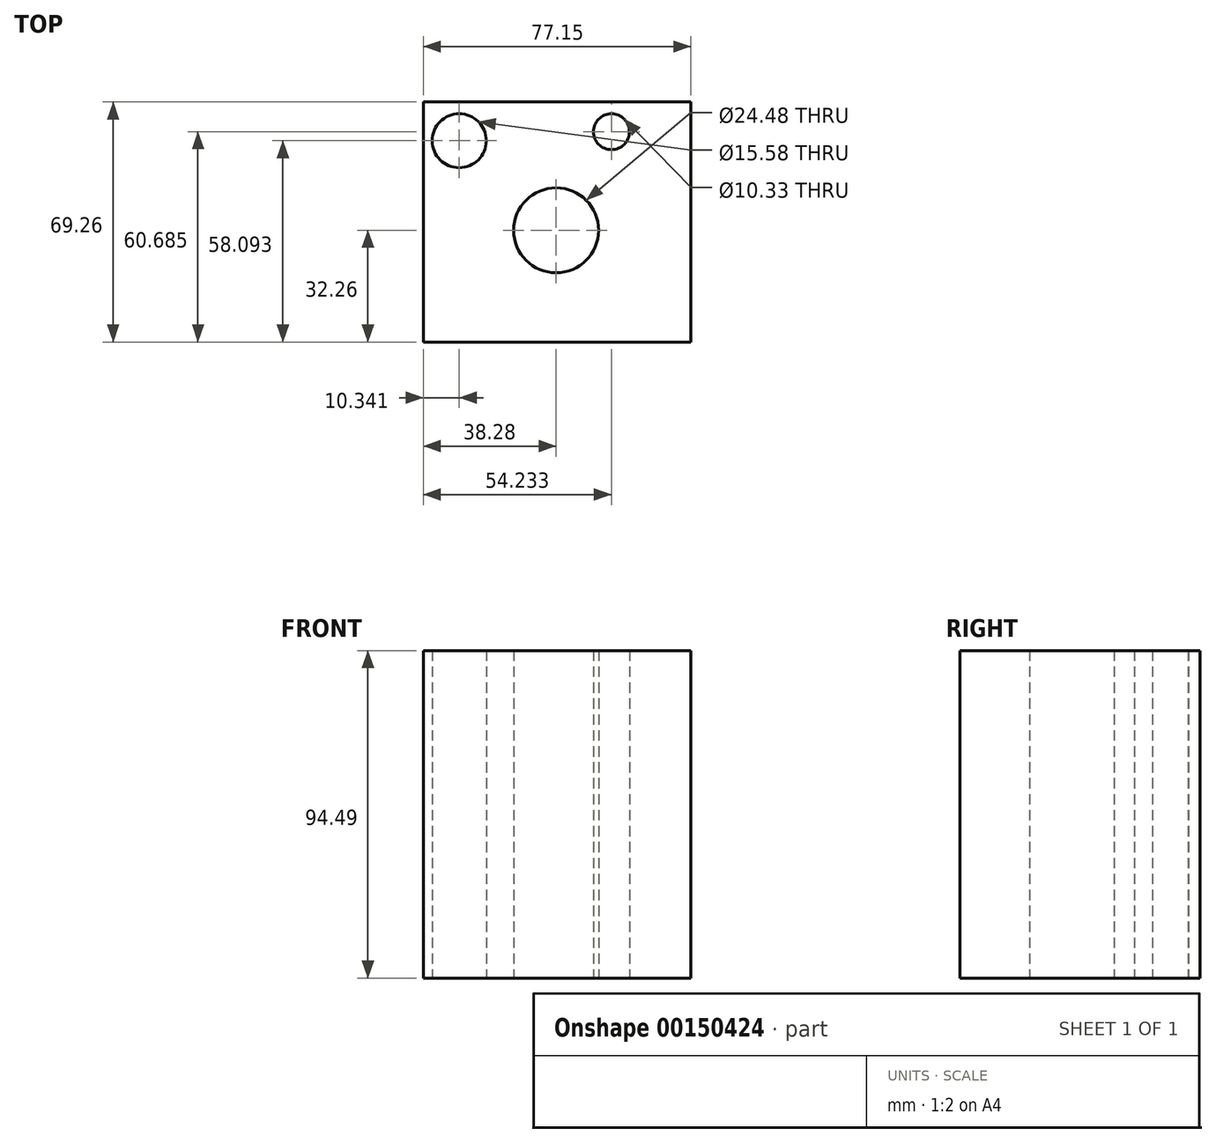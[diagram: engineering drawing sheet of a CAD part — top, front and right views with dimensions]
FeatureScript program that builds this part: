
annotation { "Feature Type Name" : "Feature", "Feature Type Description" : "" }
export const myFeature = defineFeature(function(context is Context, id is Id, definition is map)
    precondition{}
    {
        {
            var Q0;
            Q0=qCreatedBy(makeId("Top.planeOp"),FACE);
            var sketch = newSketch(context, id + "F0", { "sketchPlane" : qUnion([Q0])});
            skLineSegment(sketch, "E0.bottom", {"start": v(-38.28, 37) * mm, "end": v(38.87, 37) * mm});
            skLineSegment(sketch, "E0.top", {"start": v(-38.28, -32.26) * mm, "end": v(38.87, -32.26) * mm});
            skLineSegment(sketch, "E0.left", {"start": v(-38.28, 37) * mm, "end": v(-38.28, -32.26) * mm});
            skLineSegment(sketch, "E0.right", {"start": v(38.87, 37) * mm, "end": v(38.87, -32.26) * mm});
            skCircle(sketch, "E1", {"center": v(0, 0) * mm, "radius": 12.24 * mm});
            skCircle(sketch, "E2", {"center": v(-27.94, 25.83) * mm, "radius": 7.79 * mm});
            skCircle(sketch, "E3", {"center": v(15.95, 28.42) * mm, "radius": 5.17 * mm});
            skSolve(sketch);
        }
        {
            var Q0;
            Q0=makeQuery(id+"F0.imprint","IMPRINT",FACE,{"disambiguationData":[TD([[makeQuery(id+"F0.imprint","IMPRINT",EDGE,{"derivedFrom":sQuery(id+"F0.wireOp",EDGE,"E0.bottom")}),-1.0]])]});
            extrude(context, id + "F1", {"entities" : qUnion([Q0]), "depth" : 13.2 * mm});
        }
        {
            var Q0;
            Q0=makeQuery(id+"F1.opExtrude","CAP_FACE",FACE,{"disambiguationData":[OSD([sQuery(id+"F0.wireOp",EDGE,"E0.bottom"),sQuery(id+"F0.wireOp",EDGE,"E0.top"),sQuery(id+"F0.wireOp",EDGE,"E0.left"),sQuery(id+"F0.wireOp",EDGE,"E0.right"),sQuery(id+"F0.wireOp",EDGE,"E1")])],"isStart":false});
            extrude(context, id + "F2", {"entities" : qUnion([Q0]), "operationType" : NewBodyOperationType.ADD, "oppositeDirection" : true, "depth" : 94.49 * mm});
        }
    });
